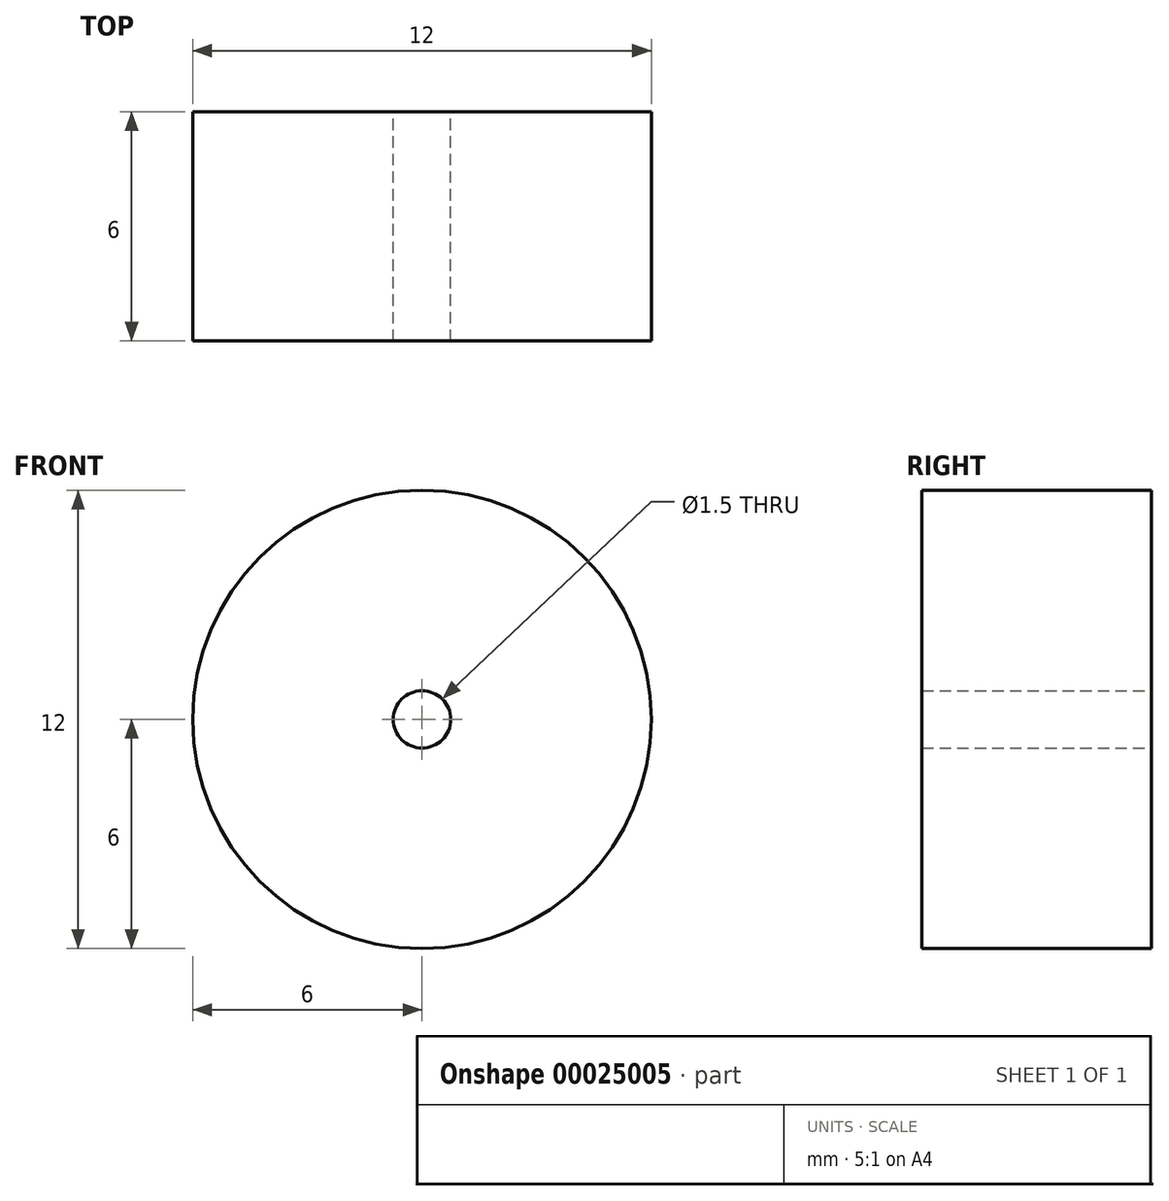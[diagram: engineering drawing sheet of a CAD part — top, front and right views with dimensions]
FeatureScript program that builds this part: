
annotation { "Feature Type Name" : "Feature", "Feature Type Description" : "" }
export const myFeature = defineFeature(function(context is Context, id is Id, definition is map)
    precondition{}
    {
        {
            var Q0;
            Q0=qCreatedBy(makeId("Front.planeOp"),FACE);
            var sketch = newSketch(context, id + "F0", { "sketchPlane" : qUnion([Q0])});
            skCircle(sketch, "E0", {"center": v(0, 0) * mm, "radius": 4.5 * mm});
            skCircle(sketch, "E1", {"center": v(0, 0) * mm, "radius": 0.75 * mm});
            skCircle(sketch, "E2", {"center": v(0, 0) * mm, "radius": 6 * mm});
            skSolve(sketch);
        }
        {
            var Q0;
            Q0 = qSketchRegion(id + "F0", true);
            var Q1;
            Q1=makeQuery(id+"F0.imprint","IMPRINT",FACE,{"disambiguationData":[TD([[makeQuery(id+"F0.imprint","IMPRINT",EDGE,{"derivedFrom":sQuery(id+"F0.wireOp",EDGE,"E0")}),1.0]])]});
            extrude(context, id + "F1", {"entities" : qUnion([Q0, Q1]), "depth" : 6 * mm});
        }
    });
